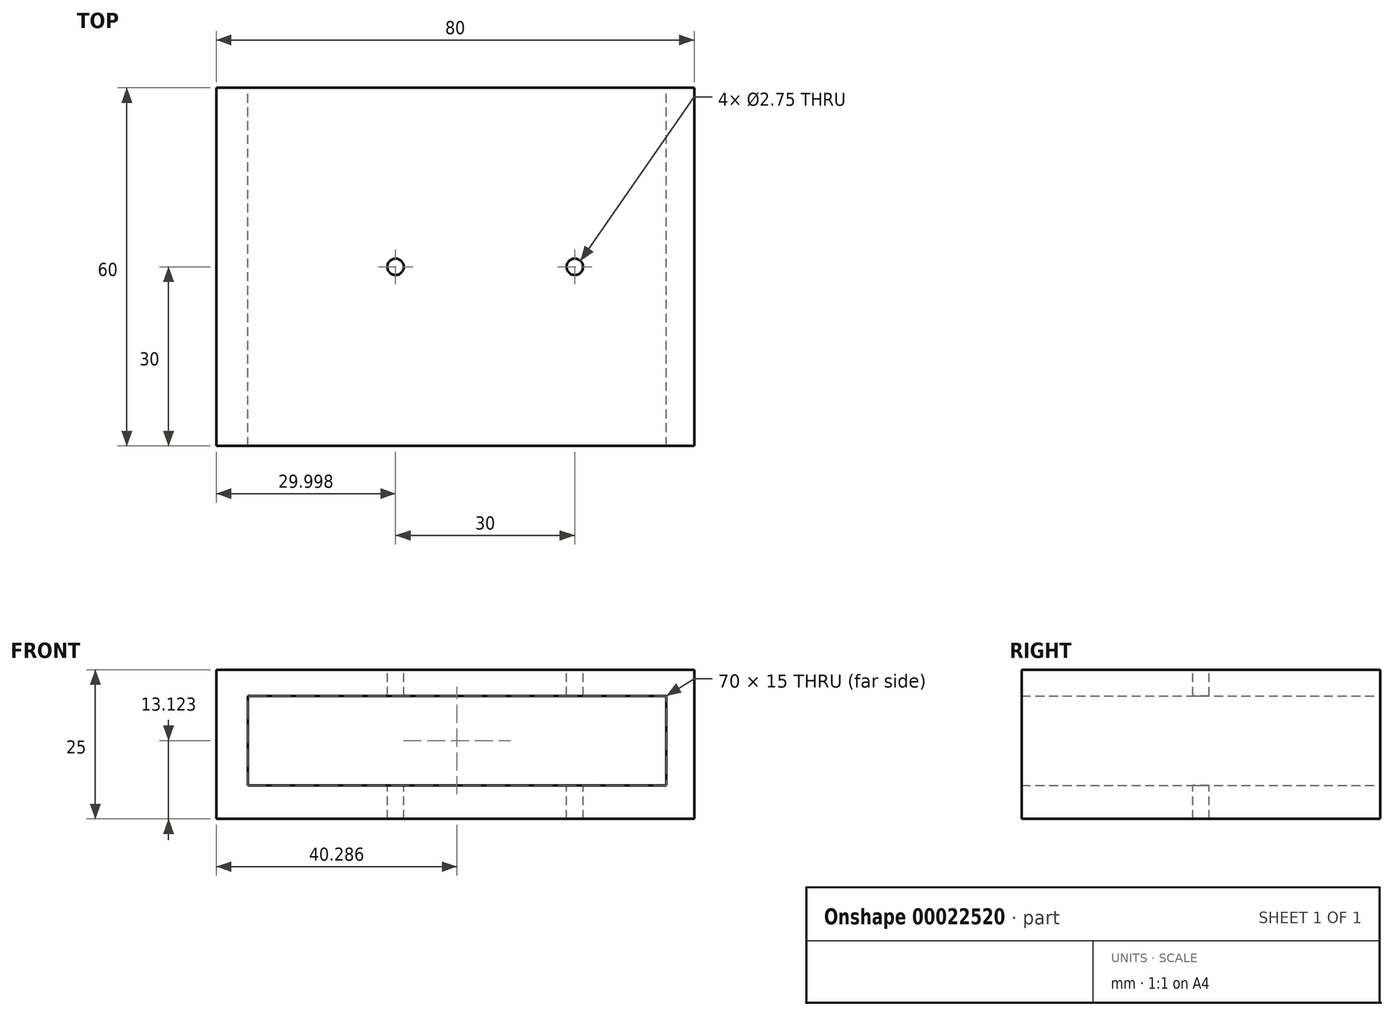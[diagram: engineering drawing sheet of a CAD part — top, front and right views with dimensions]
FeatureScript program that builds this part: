
annotation { "Feature Type Name" : "Feature", "Feature Type Description" : "" }
export const myFeature = defineFeature(function(context is Context, id is Id, definition is map)
    precondition{}
    {
        {
            var Q0;
            Q0=qCreatedBy(makeId("Top.planeOp"),FACE);
            var sketch = newSketch(context, id + "F0", { "sketchPlane" : qUnion([Q0])});
            skLineSegment(sketch, "E0.bottom", {"start": v(-20.97, 36.17) * mm, "end": v(59.03, 36.17) * mm});
            skLineSegment(sketch, "E0.top", {"start": v(-20.97, -23.83) * mm, "end": v(59.03, -23.83) * mm});
            skLineSegment(sketch, "E0.left", {"start": v(-20.97, 36.17) * mm, "end": v(-20.97, -23.83) * mm});
            skLineSegment(sketch, "E0.right", {"start": v(59.03, 36.17) * mm, "end": v(59.03, -23.83) * mm});
            skSolve(sketch);
        }
        {
            var Q0;
            Q0 = qSketchRegion(id + "F0", true);
            extrude(context, id + "F1", {"entities" : qUnion([Q0]), "depth" : 25 * mm});
        }
        {
            var Q0;
            Q0=makeQuery(id+"F1.opExtrude","SWEPT_FACE",FACE,{"disambiguationData":[OSD([sQuery(id+"F0.wireOp",EDGE,"E0.bottom")])]});
            var sketch = newSketch(context, id + "F2", { "sketchPlane" : qUnion([Q0])});
            skLineSegment(sketch, "E1.bottom", {"start": v(15.68, 20.62) * mm, "end": v(-54.32, 20.62) * mm});
            skLineSegment(sketch, "E1.top", {"start": v(15.68, 5.62) * mm, "end": v(-54.32, 5.62) * mm});
            skLineSegment(sketch, "E1.left", {"start": v(15.68, 20.62) * mm, "end": v(15.68, 5.62) * mm});
            skLineSegment(sketch, "E1.right", {"start": v(-54.32, 20.62) * mm, "end": v(-54.32, 5.62) * mm});
            skSolve(sketch);
        }
        {
            var Q0;
            Q0 = qSketchRegion(id + "F2", true);
            extrude(context, id + "F3", {"entities" : qUnion([Q0]), "operationType" : NewBodyOperationType.REMOVE, "endBound" : BoundingType.THROUGH_ALL, "oppositeDirection" : true, "depth" : 50 * mm});
        }
        {
            var Q0;
            Q0=makeQuery(id+"F1.opExtrude","CAP_FACE",FACE,{"disambiguationData":[OSD([sQuery(id+"F0.wireOp",EDGE,"E0.bottom"),sQuery(id+"F0.wireOp",EDGE,"E0.top"),sQuery(id+"F0.wireOp",EDGE,"E0.left"),sQuery(id+"F0.wireOp",EDGE,"E0.right")])],"isStart":false});
            var sketch = newSketch(context, id + "F4", { "sketchPlane" : qUnion([Q0])});
            skCircle(sketch, "E2", {"center": v(3.89, -54.58) * mm, "radius": 1.38 * mm});
            skCircle(sketch, "E3", {"center": v(99.86, -32.16) * mm, "radius": 1.38 * mm});
            skLineSegment(sketch, "E4", {"start": v(-20.97, 6.17) * mm, "end": v(9.03, 6.17) * mm});
            skLineSegment(sketch, "E5", {"start": v(59.03, 6.17) * mm, "end": v(39.03, 6.17) * mm});
            skPoint(sketch, "E6", {"position": v(9.03, 6.17) * mm});
            skPoint(sketch, "E7", {"position": v(39.03, 6.17) * mm});
            skCircle(sketch, "E8", {"center": v(9.03, 6.17) * mm, "radius": 1.38 * mm});
            skCircle(sketch, "E9", {"center": v(39.03, 6.17) * mm, "radius": 1.38 * mm});
            skSolve(sketch);
        }
        {
            var Q0;
            Q0=makeQuery(id+"F4.imprint","IMPRINT",FACE,{"disambiguationData":[TD([[makeQuery(id+"F4.imprint","IMPRINT",EDGE,{"derivedFrom":sQuery(id+"F4.wireOp",EDGE,"E8")}),1.0]])]});
            var Q1;
            Q1=makeQuery(id+"F4.imprint","IMPRINT",FACE,{"disambiguationData":[TD([[makeQuery(id+"F4.imprint","IMPRINT",EDGE,{"derivedFrom":sQuery(id+"F4.wireOp",EDGE,"E9")}),1.0]])]});
            extrude(context, id + "F5", {"entities" : qUnion([Q0, Q1]), "operationType" : NewBodyOperationType.REMOVE, "endBound" : BoundingType.THROUGH_ALL, "oppositeDirection" : true, "depth" : 25 * mm});
        }
    });
